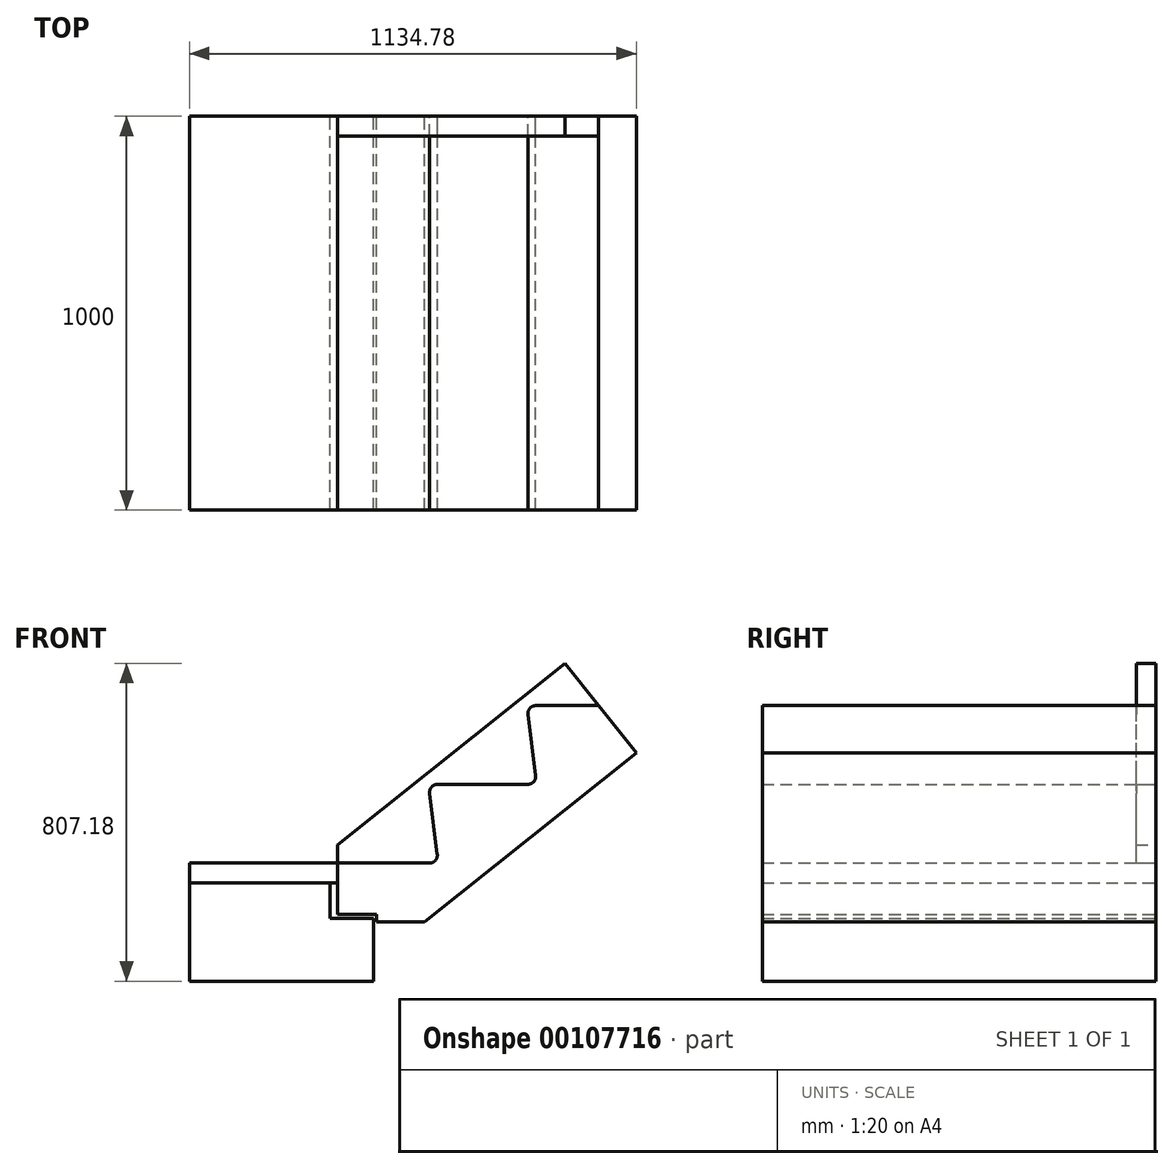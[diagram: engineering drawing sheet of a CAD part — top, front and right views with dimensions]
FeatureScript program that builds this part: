
annotation { "Feature Type Name" : "Feature", "Feature Type Description" : "" }
export const myFeature = defineFeature(function(context is Context, id is Id, definition is map)
    precondition{}
    {
        {
            var Q0;
            Q0=qCreatedBy(makeId("Front.planeOp"),FACE);
            var sketch = newSketch(context, id + "F0", { "sketchPlane" : qUnion([Q0])});
            skLineSegment(sketch, "E0", {"start": v(-254.34, -90.5) * mm, "end": v(-21.24, -90.5) * mm});
            skLineSegment(sketch, "E1", {"start": v(-1.4, -68.01) * mm, "end": v(-20.77, 87.03) * mm});
            skLineSegment(sketch, "E2", {"start": v(-254.34, -44.84) * mm, "end": v(322.56, 416.69) * mm});
            skLineSegment(sketch, "E3", {"start": v(-33.4, -240.5) * mm, "end": v(504.15, 189.55) * mm});
            skLineSegment(sketch, "E4", {"start": v(-254.34, -90.5) * mm, "end": v(-630.63, -90.5) * mm});
            skLineSegment(sketch, "E5", {"start": v(-163.4, -390.5) * mm, "end": v(-630.63, -390.5) * mm});
            skLineSegment(sketch, "E6", {"start": v(-33.4, -240.5) * mm, "end": v(-155.43, -240.5) * mm});
            skLineSegment(sketch, "E7", {"start": v(-0.92, 109.5) * mm, "end": v(228.76, 109.5) * mm});
            skLineSegment(sketch, "E8", {"start": v(248.6, 131.99) * mm, "end": v(229.23, 287.03) * mm});
            skLineSegment(sketch, "E9", {"start": v(249.08, 309.5) * mm, "end": v(408.25, 309.5) * mm});
            skLineSegment(sketch, "E10", {"start": v(-163.4, -230.5) * mm, "end": v(-163.4, -390.5) * mm});
            skLineSegment(sketch, "E11", {"start": v(-273.58, -230.5) * mm, "end": v(-273.58, -140.5) * mm});
            skLineSegment(sketch, "E12", {"start": v(-254.34, -140.5) * mm, "end": v(-630.63, -140.5) * mm});
            skLineSegment(sketch, "E13", {"start": v(-155.43, -240.5) * mm, "end": v(-155.43, -220.5) * mm});
            skLineSegment(sketch, "E14", {"start": v(-155.43, -220.5) * mm, "end": v(-254.34, -220.5) * mm});
            skLineSegment(sketch, "E15", {"start": v(-163.4, -230.5) * mm, "end": v(-273.58, -230.5) * mm});
            skLineSegment(sketch, "E16", {"start": v(-254.34, -220.5) * mm, "end": v(-254.34, -44.84) * mm});
            skLineSegment(sketch, "E17", {"start": v(-254.34, -220.5) * mm, "end": v(-254.34, -90.5) * mm});
            skLineSegment(sketch, "E18", {"start": v(260.59, 494.21) * mm, "end": v(630.63, 31.33) * mm});
            skLineSegment(sketch, "E19", {"start": v(-630.63, 35.95) * mm, "end": v(-630.63, -494.21) * mm});
            skArc(sketch, "E20", {"start": v(-21.24, -90.5) * mm, "mid": v(-6.24, -83.73) * mm, "end": v(-1.4, -68.01) * mm});
            skArc(sketch, "E21", {"start": v(-0.92, 109.5) * mm, "mid": v(-15.92, 102.74) * mm, "end": v(-20.77, 87.03) * mm});
            skArc(sketch, "E22", {"start": v(228.76, 109.5) * mm, "mid": v(243.76, 116.27) * mm, "end": v(248.6, 131.99) * mm});
            skArc(sketch, "E23", {"start": v(249.08, 309.5) * mm, "mid": v(234.08, 302.74) * mm, "end": v(229.23, 287.03) * mm});
            skLineSegment(sketch, "E24", {"start": v(-163.4, -390.5) * mm, "end": v(592.58, -390.5) * mm});
            skLineSegment(sketch, "E25", {"start": v(154.1, -90.5) * mm, "end": v(592.58, -90.5) * mm});
            skLineSegment(sketch, "E26", {"start": v(592.58, -32.21) * mm, "end": v(592.58, -444.23) * mm});
            skSolve(sketch);
        }
        {
            var Q0;
            {var subQ6=sQuery(id+"F0.wireOp",EDGE,"E0");Q0=makeQuery(id+"F0.imprint","IMPRINT",FACE,{"disambiguationData":[TD([[makeQuery(id+"F0.imprint","IMPRINT",EDGE,{"derivedFrom":subQ6}),-1.0]])]});}
            extrude(context, id + "F1", {"entities" : qUnion([Q0]), "depth" : 1000 * mm});
        }
        {
            var Q0;
            Q0=makeQuery(id+"F0.imprint","IMPRINT",FACE,{"disambiguationData":[TD([[makeQuery(id+"F0.imprint","IMPRINT",EDGE,{"derivedFrom":sQuery(id+"F0.wireOp",EDGE,"E0")}),1.0]])]});
            extrude(context, id + "F2", {"entities" : qUnion([Q0]), "depth" : 50 * mm});
        }
        {
            var Q0;
            {var subQ4=sQuery(id+"F0.wireOp",EDGE,"E5");Q0=makeQuery(id+"F0.imprint","IMPRINT",FACE,{"disambiguationData":[TD([[makeQuery(id+"F0.imprint","IMPRINT",EDGE,{"derivedFrom":subQ4}),-1.0]])]});}
            extrude(context, id + "F3", {"entities" : qUnion([Q0]), "depth" : 1000 * mm});
        }
        {
            var Q0;
            {var subQ6=sQuery(id+"F0.wireOp",EDGE,"E4");Q0=makeQuery(id+"F0.imprint","IMPRINT",FACE,{"disambiguationData":[TD([[makeQuery(id+"F0.imprint","IMPRINT",EDGE,{"derivedFrom":subQ6}),1.0]])]});}
            extrude(context, id + "F4", {"entities" : qUnion([Q0]), "depth" : 1000 * mm});
        }
    });
